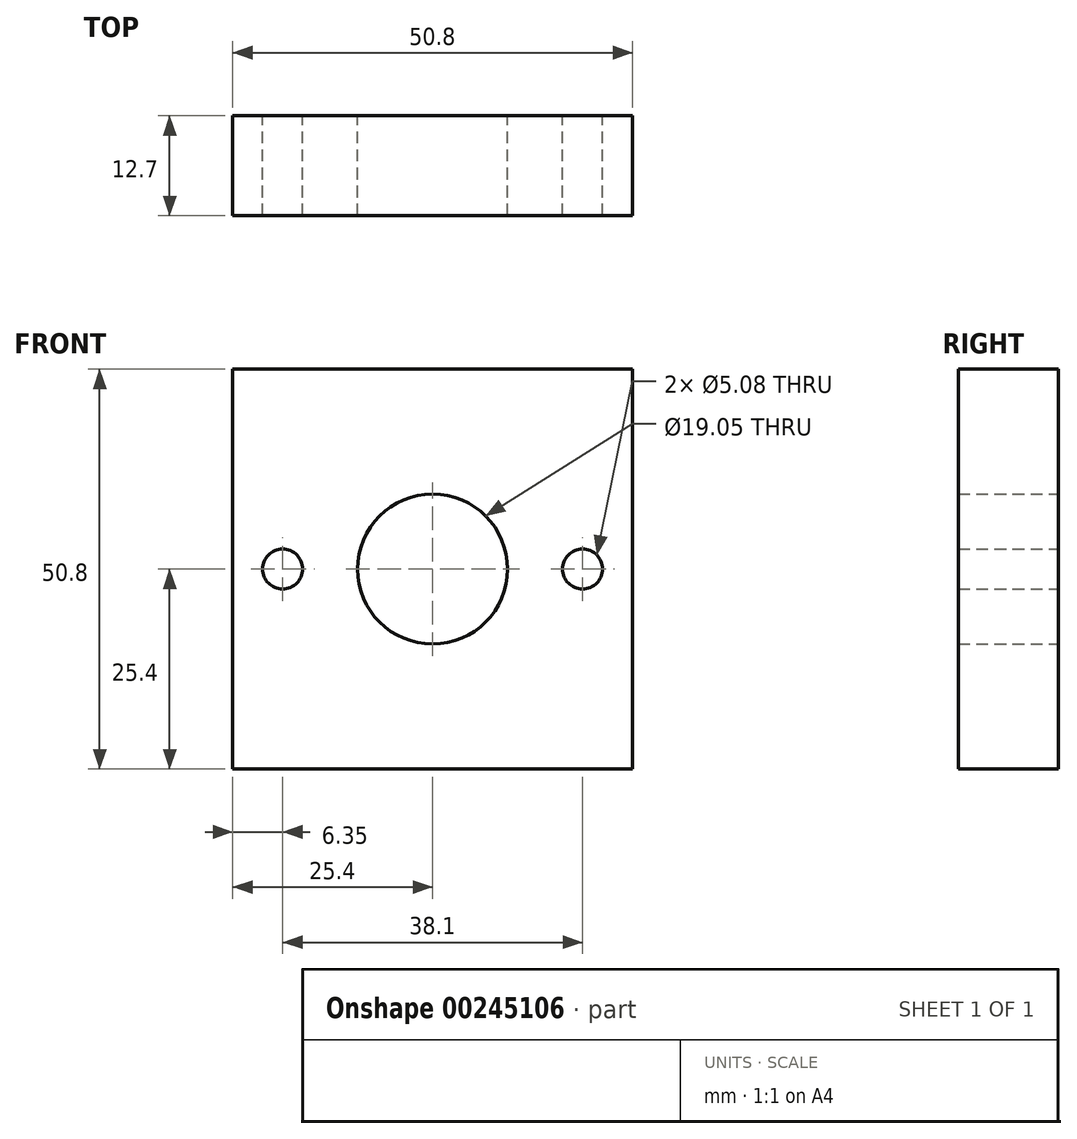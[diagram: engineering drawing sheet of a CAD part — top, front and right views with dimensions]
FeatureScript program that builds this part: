
annotation { "Feature Type Name" : "Feature", "Feature Type Description" : "" }
export const myFeature = defineFeature(function(context is Context, id is Id, definition is map)
    precondition{}
    {
        {
            var Q0;
            Q0=qCreatedBy(makeId("Front.planeOp"),FACE);
            var sketch = newSketch(context, id + "F0", { "sketchPlane" : qUnion([Q0])});
            skCircle(sketch, "E0", {"center": v(0, 0) * mm, "radius": 9.53 * mm});
            skCircle(sketch, "E1", {"center": v(-19.05, 0) * mm, "radius": 2.54 * mm});
            skCircle(sketch, "E2", {"center": v(19.05, 0) * mm, "radius": 2.54 * mm});
            skLineSegment(sketch, "E3.bottom", {"start": v(25.4, 25.4) * mm, "end": v(-25.4, 25.4) * mm});
            skLineSegment(sketch, "E3.top", {"start": v(25.4, -25.4) * mm, "end": v(-25.4, -25.4) * mm});
            skLineSegment(sketch, "E3.left", {"start": v(25.4, 25.4) * mm, "end": v(25.4, -25.4) * mm});
            skLineSegment(sketch, "E3.right", {"start": v(-25.4, 25.4) * mm, "end": v(-25.4, -25.4) * mm});
            skSolve(sketch);
        }
        {
            var Q0;
            Q0=makeQuery(id+"F0.imprint","IMPRINT",FACE,{"disambiguationData":[TD([[makeQuery(id+"F0.imprint","IMPRINT",EDGE,{"derivedFrom":sQuery(id+"F0.wireOp",EDGE,"E0")}),-1.0]])]});
            extrude(context, id + "F1", {"entities" : qUnion([Q0]), "depth" : 12.7 * mm});
        }
    });
